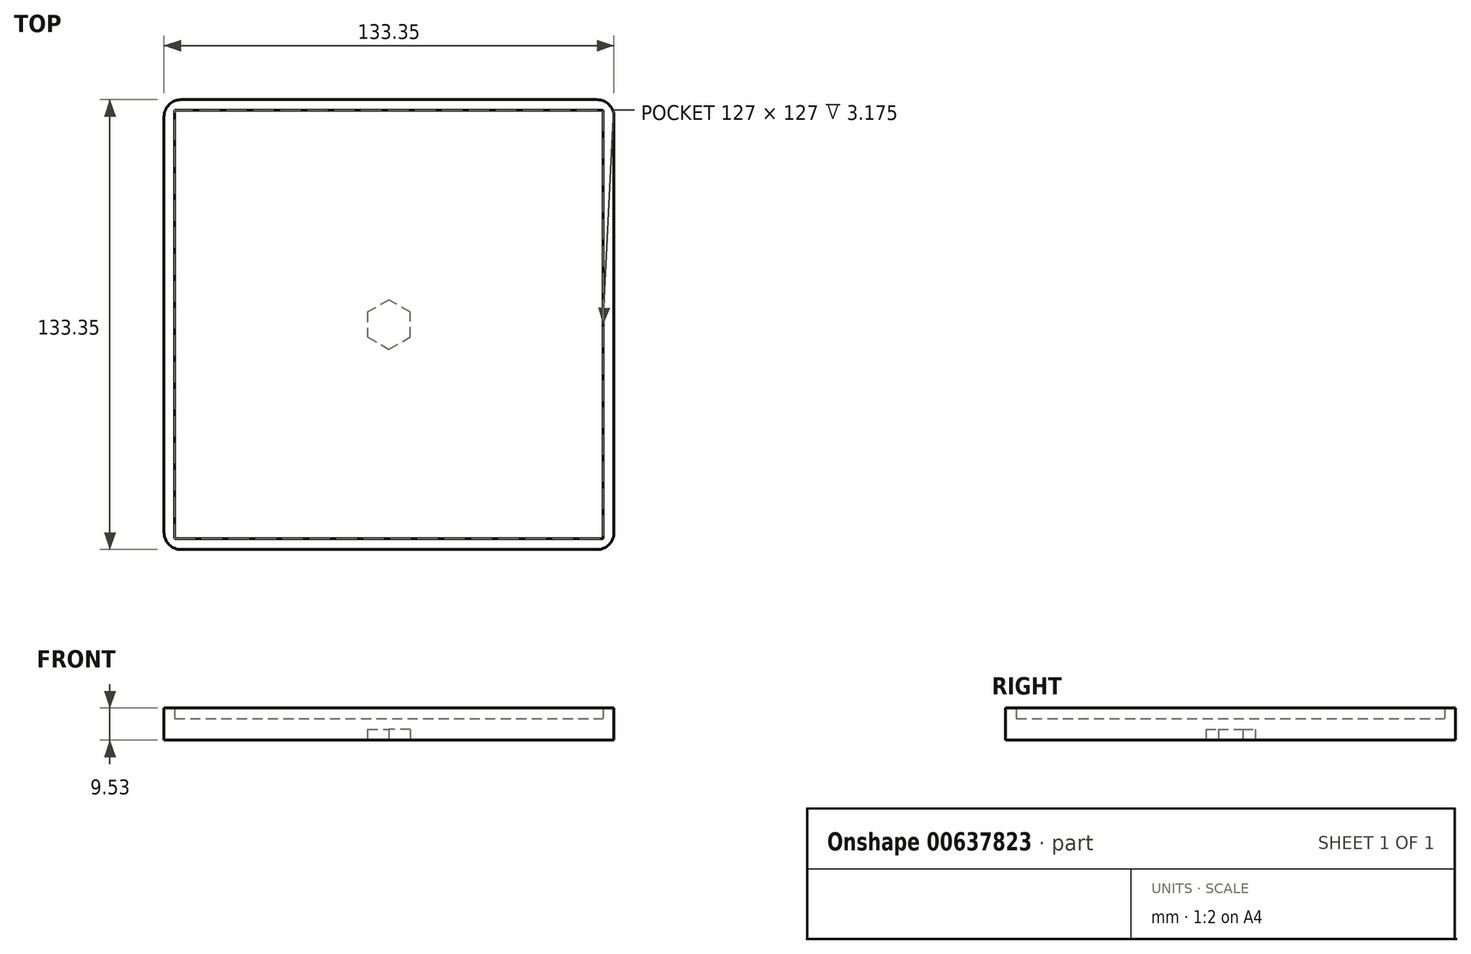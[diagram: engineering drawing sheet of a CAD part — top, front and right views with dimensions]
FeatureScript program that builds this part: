
annotation { "Feature Type Name" : "Feature", "Feature Type Description" : "" }
export const myFeature = defineFeature(function(context is Context, id is Id, definition is map)
    precondition{}
    {
        {
            var Q0;
            Q0=qCreatedBy(makeId("Top.planeOp"),FACE);
            var sketch = newSketch(context, id + "F0", { "sketchPlane" : qUnion([Q0])});
            skLineSegment(sketch, "E0.bottom", {"start": v(0, 0) * mm, "end": v(133.35, 0) * mm});
            skLineSegment(sketch, "E0.top", {"start": v(0, -133.35) * mm, "end": v(133.35, -133.35) * mm});
            skLineSegment(sketch, "E0.left", {"start": v(0, 0) * mm, "end": v(0, -133.35) * mm});
            skLineSegment(sketch, "E0.right", {"start": v(133.35, 0) * mm, "end": v(133.35, -133.35) * mm});
            skSolve(sketch);
        }
        {
            var Q0;
            Q0 = qSketchRegion(id + "F0", true);
            extrude(context, id + "F1", {"entities" : qUnion([Q0]), "depth" : 6.35 * mm, "offsetDistance" : 25.4 * mm});
        }
        {
            var Q0;
            Q0=makeQuery(id+"F1.opExtrude","CAP_FACE",FACE,{"disambiguationData":[OSD([sQuery(id+"F0.wireOp",EDGE,"E0.bottom"),sQuery(id+"F0.wireOp",EDGE,"E0.top"),sQuery(id+"F0.wireOp",EDGE,"E0.left"),sQuery(id+"F0.wireOp",EDGE,"E0.right")])],"isStart":false});
            var sketch = newSketch(context, id + "F2", { "sketchPlane" : qUnion([Q0])});
            skLineSegment(sketch, "E1.bottom", {"start": v(0, -133.35) * mm, "end": v(133.35, -133.35) * mm});
            skLineSegment(sketch, "E1.top", {"start": v(0, 0) * mm, "end": v(133.35, 0) * mm});
            skLineSegment(sketch, "E1.left", {"start": v(0, -133.35) * mm, "end": v(0, 0) * mm});
            skLineSegment(sketch, "E1.right", {"start": v(133.35, -133.35) * mm, "end": v(133.35, 0) * mm});
            skLineSegment(sketch, "E2.bottom", {"start": v(3.17, -130.17) * mm, "end": v(130.18, -130.17) * mm});
            skLineSegment(sketch, "E2.top", {"start": v(3.17, -3.18) * mm, "end": v(130.18, -3.18) * mm});
            skLineSegment(sketch, "E2.left", {"start": v(3.18, -130.17) * mm, "end": v(3.17, -3.17) * mm});
            skLineSegment(sketch, "E2.right", {"start": v(130.18, -130.17) * mm, "end": v(130.18, -3.17) * mm});
            skSolve(sketch);
        }
        {
            var Q0;
            Q0 = qSketchRegion(id + "F2", true);
            extrude(context, id + "F3", {"entities" : qUnion([Q0]), "operationType" : NewBodyOperationType.ADD, "depth" : 3.17 * mm, "offsetDistance" : 25.4 * mm});
        }
        {
            var Q0;
            Q0=makeQuery(id+"F1.opExtrude","CAP_FACE",FACE,{"disambiguationData":[OSD([sQuery(id+"F0.wireOp",EDGE,"E0.bottom"),sQuery(id+"F0.wireOp",EDGE,"E0.top"),sQuery(id+"F0.wireOp",EDGE,"E0.left"),sQuery(id+"F0.wireOp",EDGE,"E0.right")])],"isStart":true});
            var sketch = newSketch(context, id + "F4", { "sketchPlane" : qUnion([Q0])});
            skLineSegment(sketch, "E3", {"start": v(0, 133.35) * mm, "end": v(133.35, 0) * mm});
            skLineSegment(sketch, "E4", {"start": v(133.35, 133.35) * mm, "end": v(0, 0) * mm});
            skSolve(sketch);
        }
        {
            var Q0;
            {var subQ1=makeQuery(id+"F1.opExtrude","CAP_EDGE",EDGE,{"disambiguationData":[OSD([sQuery(id+"F0.wireOp",EDGE,"E0.right")])],"isStart":true});Q0=makeQuery(id+"F4.imprint","IMPRINT",FACE,{"disambiguationData":[TD([[makeQuery(id+"F4.imprint","IMPRINT",EDGE,{"derivedFrom":subQ1}),1.0]])]});}
            var sketch = newSketch(context, id + "F5", { "sketchPlane" : qUnion([Q0])});
            skCircle(sketch, "E5.cCircle", {"center": v(66.68, 66.67) * mm, "radius": 6.35 * mm, "construction": true});
            skLineSegment(sketch, "E5.0", {"start": v(73.03, 70.34) * mm, "end": v(73.03, 63) * mm});
            skLineSegment(sketch, "E5.1", {"start": v(73.03, 63) * mm, "end": v(66.68, 59.34) * mm});
            skLineSegment(sketch, "E5.2", {"start": v(66.68, 59.34) * mm, "end": v(60.33, 63) * mm});
            skLineSegment(sketch, "E5.3", {"start": v(60.33, 63) * mm, "end": v(60.33, 70.34) * mm});
            skLineSegment(sketch, "E5.4", {"start": v(60.33, 70.34) * mm, "end": v(66.68, 74) * mm});
            skLineSegment(sketch, "E5.5", {"start": v(66.68, 74) * mm, "end": v(73.03, 70.34) * mm});
            skPoint(sketch, "E5.0.midPoint", {"position": v(73.03, 66.67) * mm});
            skSolve(sketch);
        }
        {
            var Q0;
            Q0 = qSketchRegion(id + "F5", true);
            extrude(context, id + "F6", {"entities" : qUnion([Q0]), "operationType" : NewBodyOperationType.REMOVE, "oppositeDirection" : true, "depth" : 3.17 * mm, "offsetDistance" : 25.4 * mm});
        }
        {
            var Q0;
            Q0=makeQuery(id+"F3.boolean.opBoolean","MERGE",EDGE,{"derivedFrom":[makeQuery(id+"F1.opExtrude","SWEPT_EDGE",EDGE,{"disambiguationData":[OSD([sQuery(id+"F0.wireOp",EDGE,"E0.top"),sQuery(id+"F0.wireOp",EDGE,"E0.right")])]}),makeQuery(id+"F3.opExtrude","SWEPT_EDGE",EDGE,{"disambiguationData":[OSD([sQuery(id+"F2.wireOp",EDGE,"E1.bottom"),sQuery(id+"F2.wireOp",EDGE,"E1.right")])]})]});
            var Q1;
            Q1=makeQuery(id+"F3.boolean.opBoolean","MERGE",EDGE,{"derivedFrom":[makeQuery(id+"F1.opExtrude","SWEPT_EDGE",EDGE,{"disambiguationData":[OSD([sQuery(id+"F0.wireOp",EDGE,"E0.bottom"),sQuery(id+"F0.wireOp",EDGE,"E0.right")])]}),makeQuery(id+"F3.opExtrude","SWEPT_EDGE",EDGE,{"disambiguationData":[OSD([sQuery(id+"F2.wireOp",EDGE,"E1.top"),sQuery(id+"F2.wireOp",EDGE,"E1.right")])]})]});
            var Q2;
            Q2=makeQuery(id+"F3.boolean.opBoolean","MERGE",EDGE,{"derivedFrom":[makeQuery(id+"F1.opExtrude","SWEPT_EDGE",EDGE,{"disambiguationData":[OSD([sQuery(id+"F0.wireOp",EDGE,"E0.bottom"),sQuery(id+"F0.wireOp",EDGE,"E0.left")])]}),makeQuery(id+"F3.opExtrude","SWEPT_EDGE",EDGE,{"disambiguationData":[OSD([sQuery(id+"F2.wireOp",EDGE,"E1.top"),sQuery(id+"F2.wireOp",EDGE,"E1.left")])]})]});
            var Q3;
            Q3=makeQuery(id+"F3.boolean.opBoolean","MERGE",EDGE,{"derivedFrom":[makeQuery(id+"F1.opExtrude","SWEPT_EDGE",EDGE,{"disambiguationData":[OSD([sQuery(id+"F0.wireOp",EDGE,"E0.top"),sQuery(id+"F0.wireOp",EDGE,"E0.left")])]}),makeQuery(id+"F3.opExtrude","SWEPT_EDGE",EDGE,{"disambiguationData":[OSD([sQuery(id+"F2.wireOp",EDGE,"E1.bottom"),sQuery(id+"F2.wireOp",EDGE,"E1.left")])]})]});
            fillet(context, id + "F7", {"entities" : qUnion([Q0, Q1, Q2, Q3]), "radius" : 5.08 * mm, "tangentPropagation" : true, "allowEdgeOverflow" : false});
        }
    });
